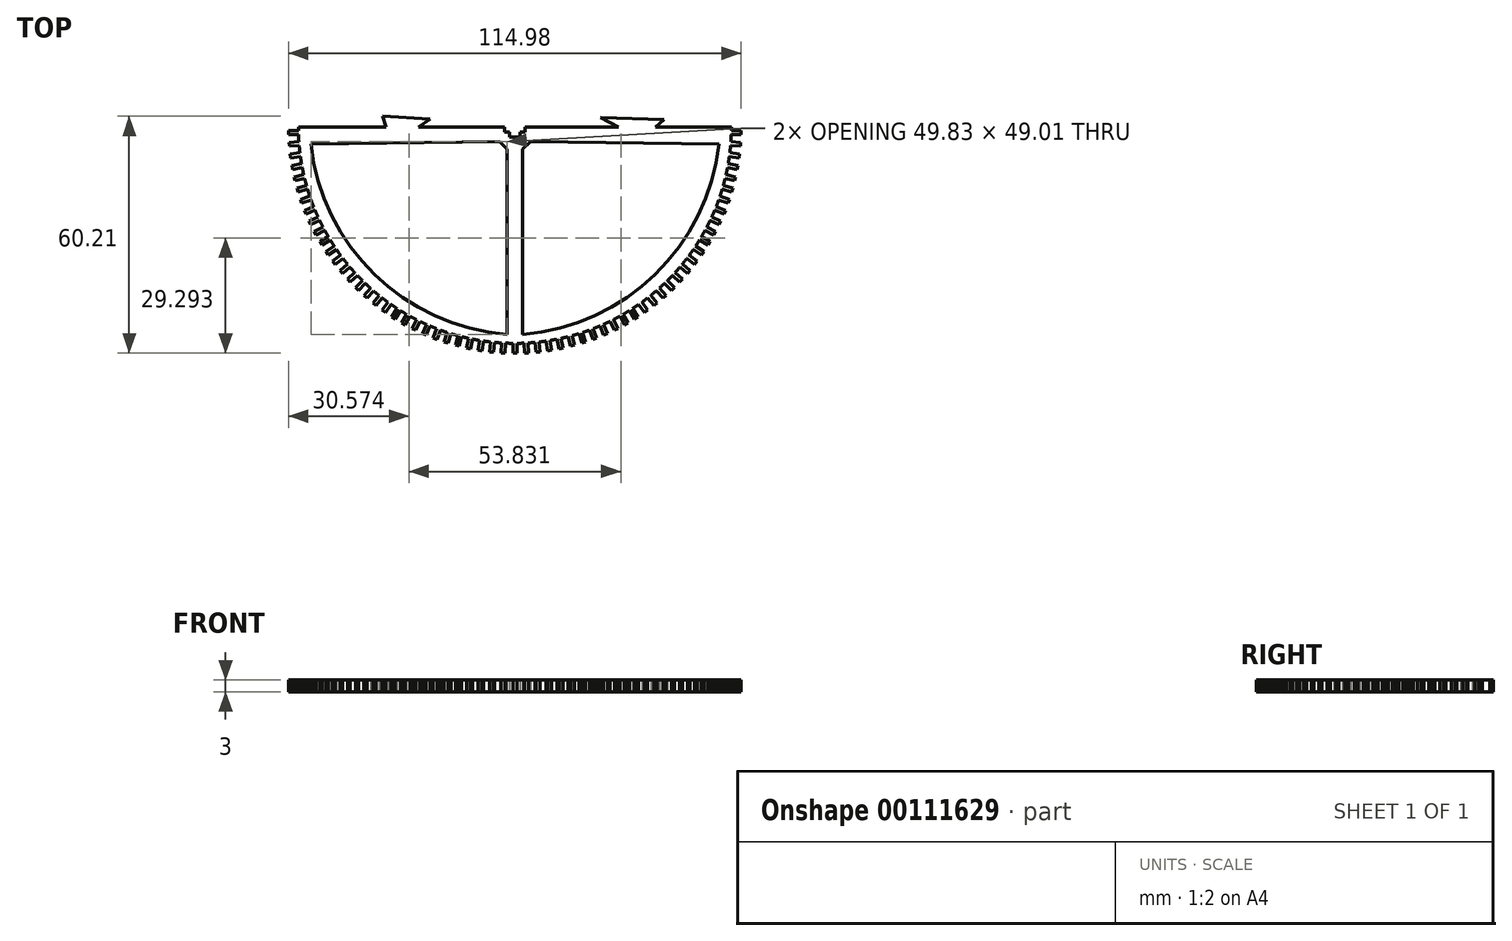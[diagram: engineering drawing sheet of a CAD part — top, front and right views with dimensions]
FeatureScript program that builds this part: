
annotation { "Feature Type Name" : "Feature", "Feature Type Description" : "" }
export const myFeature = defineFeature(function(context is Context, id is Id, definition is map)
    precondition{}
    {
        {
            var Q0;
            Q0=qCreatedBy(makeId("Top.planeOp"),FACE);
            var sketch = newSketch(context, id + "F0", { "sketchPlane" : qUnion([Q0])});
            skArc(sketch, "E0", {"start": v(-55, -0.92) * mm, "mid": v(0, -55) * mm, "end": v(55, -0.92) * mm});
            skLineSegment(sketch, "E1", {"start": v(2.6, -1.3) * mm, "end": v(1.3, -1.3) * mm});
            skLineSegment(sketch, "E2", {"start": v(1.3, -1.3) * mm, "end": v(1.3, -2.6) * mm});
            skLineSegment(sketch, "E3", {"start": v(1.3, -2.6) * mm, "end": v(0, -2.6) * mm});
            skLineSegment(sketch, "E4", {"start": v(0, -2.6) * mm, "end": v(-1.3, -2.6) * mm});
            skLineSegment(sketch, "E5", {"start": v(-1.3, -2.6) * mm, "end": v(-1.3, -1.3) * mm});
            skLineSegment(sketch, "E6", {"start": v(-1.3, -1.3) * mm, "end": v(-2.6, -1.3) * mm});
            skLineSegment(sketch, "E7", {"start": v(-2.6, -1.3) * mm, "end": v(-2.6, 0) * mm});
            skLineSegment(sketch, "E8", {"start": v(-3.92, -3.7) * mm, "end": v(-2, -5.66) * mm});
            skPoint(sketch, "E9.end.orphan", {"position": v(-1.3, -51.23) * mm});
            skPoint(sketch, "E9.start.orphan", {"position": v(0, -51.23) * mm});
            skLineSegment(sketch, "E10", {"start": v(-2, -50.71) * mm, "end": v(-2, -5.66) * mm});
            skPoint(sketch, "E11.start.orphan", {"position": v(0, -50.71) * mm});
            skLineSegment(sketch, "E12", {"start": v(-2, -50.71) * mm, "end": v(-2, -52.71) * mm});
            skArc(sketch, "E13", {"start": v(-51.83, -4.33) * mm, "mid": v(-35.63, -37.5) * mm, "end": v(-2, -52.71) * mm});
            skPoint(sketch, "E14.end.orphan", {"position": v(2, -50.71) * mm});
            skPoint(sketch, "E15.start.orphan", {"position": v(-51.96, 0) * mm});
            skLineSegment(sketch, "E16", {"start": v(-3.92, -3.7) * mm, "end": v(-51.83, -4.33) * mm});
            skPoint(sketch, "E16.endSnap0", {"position": v(-3.3, -4.33) * mm});
            skPoint(sketch, "E17.orphan", {"position": v(-4.62, -3) * mm});
            skLineSegment(sketch, "E18.MirrorCS", {"start": v(3.92, -3.7) * mm, "end": v(51.83, -4.33) * mm});
            skArc(sketch, "E19.MirrorCS", {"start": v(51.83, -4.33) * mm, "mid": v(35.63, -37.5) * mm, "end": v(2, -52.71) * mm});
            skLineSegment(sketch, "E20.MirrorCS", {"start": v(2, -50.71) * mm, "end": v(2, -5.66) * mm});
            skLineSegment(sketch, "E21.MirrorCS", {"start": v(3.92, -3.7) * mm, "end": v(2, -5.66) * mm});
            skLineSegment(sketch, "E22.MirrorCS", {"start": v(2, -50.71) * mm, "end": v(2, -52.71) * mm});
            skLineSegment(sketch, "E23.2.31.0", {"start": v(-57.5, -0.98) * mm, "end": v(-55, -0.92) * mm});
            skLineSegment(sketch, "E23.3.31.0", {"start": v(-57.47, -1.98) * mm, "end": v(-54.97, -1.92) * mm});
            skLineSegment(sketch, "E23.6.31.0", {"start": v(-57.48, -1.48) * mm, "end": v(-57.47, -1.98) * mm});
            skLineSegment(sketch, "E23.9.31.0", {"start": v(-57.48, -1.48) * mm, "end": v(-57.5, -0.98) * mm});
            skLineSegment(sketch, "E23.2.32.0", {"start": v(-57.37, -3.94) * mm, "end": v(-54.87, -3.75) * mm});
            skLineSegment(sketch, "E23.3.32.0", {"start": v(-57.29, -4.94) * mm, "end": v(-54.8, -4.74) * mm});
            skLineSegment(sketch, "E23.6.32.0", {"start": v(-57.33, -4.44) * mm, "end": v(-57.29, -4.94) * mm});
            skLineSegment(sketch, "E23.9.32.0", {"start": v(-57.33, -4.44) * mm, "end": v(-57.37, -3.94) * mm});
            skLineSegment(sketch, "E23.2.33.0", {"start": v(-57.09, -6.89) * mm, "end": v(-54.6, -6.57) * mm});
            skLineSegment(sketch, "E23.3.33.0", {"start": v(-56.96, -7.88) * mm, "end": v(-54.48, -7.56) * mm});
            skLineSegment(sketch, "E23.6.33.0", {"start": v(-57.02, -7.38) * mm, "end": v(-56.96, -7.88) * mm});
            skLineSegment(sketch, "E23.9.33.0", {"start": v(-57.02, -7.38) * mm, "end": v(-57.09, -6.89) * mm});
            skLineSegment(sketch, "E23.2.34.0", {"start": v(-56.66, -9.82) * mm, "end": v(-54.2, -9.37) * mm});
            skLineSegment(sketch, "E23.3.34.0", {"start": v(-56.48, -10.8) * mm, "end": v(-54.02, -10.35) * mm});
            skLineSegment(sketch, "E23.6.34.0", {"start": v(-56.57, -10.3) * mm, "end": v(-56.48, -10.8) * mm});
            skLineSegment(sketch, "E23.9.34.0", {"start": v(-56.57, -10.3) * mm, "end": v(-56.66, -9.82) * mm});
            skLineSegment(sketch, "E23.2.35.0", {"start": v(-56.08, -12.72) * mm, "end": v(-53.64, -12.15) * mm});
            skLineSegment(sketch, "E23.3.35.0", {"start": v(-55.85, -13.7) * mm, "end": v(-53.41, -13.12) * mm});
            skLineSegment(sketch, "E23.6.35.0", {"start": v(-55.96, -13.2) * mm, "end": v(-55.85, -13.7) * mm});
            skLineSegment(sketch, "E23.9.35.0", {"start": v(-55.96, -13.2) * mm, "end": v(-56.08, -12.72) * mm});
            skLineSegment(sketch, "E23.2.36.0", {"start": v(-55.35, -15.6) * mm, "end": v(-52.95, -14.9) * mm});
            skLineSegment(sketch, "E23.3.36.0", {"start": v(-55.07, -16.55) * mm, "end": v(-52.67, -15.85) * mm});
            skLineSegment(sketch, "E23.6.36.0", {"start": v(-55.2, -16.07) * mm, "end": v(-55.07, -16.55) * mm});
            skLineSegment(sketch, "E23.9.36.0", {"start": v(-55.2, -16.07) * mm, "end": v(-55.35, -15.6) * mm});
            skLineSegment(sketch, "E23.2.37.0", {"start": v(-54.47, -18.42) * mm, "end": v(-52.1, -17.6) * mm});
            skLineSegment(sketch, "E23.3.37.0", {"start": v(-54.14, -19.36) * mm, "end": v(-51.78, -18.54) * mm});
            skLineSegment(sketch, "E23.6.37.0", {"start": v(-54.3, -18.9) * mm, "end": v(-54.14, -19.36) * mm});
            skLineSegment(sketch, "E23.9.37.0", {"start": v(-54.3, -18.9) * mm, "end": v(-54.47, -18.42) * mm});
            skLineSegment(sketch, "E23.2.38.0", {"start": v(-53.45, -21.2) * mm, "end": v(-51.13, -20.26) * mm});
            skLineSegment(sketch, "E23.3.38.0", {"start": v(-53.08, -22.13) * mm, "end": v(-50.76, -21.18) * mm});
            skLineSegment(sketch, "E23.6.38.0", {"start": v(-53.26, -21.66) * mm, "end": v(-53.08, -22.13) * mm});
            skLineSegment(sketch, "E23.9.38.0", {"start": v(-53.26, -21.66) * mm, "end": v(-53.45, -21.2) * mm});
            skLineSegment(sketch, "E23.2.39.0", {"start": v(-52.29, -23.92) * mm, "end": v(-50.02, -22.86) * mm});
            skLineSegment(sketch, "E23.3.39.0", {"start": v(-51.87, -24.83) * mm, "end": v(-49.6, -23.77) * mm});
            skLineSegment(sketch, "E23.6.39.0", {"start": v(-52.08, -24.38) * mm, "end": v(-51.87, -24.83) * mm});
            skLineSegment(sketch, "E23.9.39.0", {"start": v(-52.08, -24.38) * mm, "end": v(-52.29, -23.92) * mm});
            skLineSegment(sketch, "E23.2.40.0", {"start": v(-50.99, -26.58) * mm, "end": v(-48.78, -25.4) * mm});
            skLineSegment(sketch, "E23.3.40.0", {"start": v(-50.52, -27.47) * mm, "end": v(-48.31, -26.29) * mm});
            skLineSegment(sketch, "E23.6.40.0", {"start": v(-50.75, -27.02) * mm, "end": v(-50.52, -27.47) * mm});
            skLineSegment(sketch, "E23.9.40.0", {"start": v(-50.75, -27.02) * mm, "end": v(-50.99, -26.58) * mm});
            skLineSegment(sketch, "E23.2.41.0", {"start": v(-49.55, -29.17) * mm, "end": v(-47.4, -27.88) * mm});
            skLineSegment(sketch, "E23.3.41.0", {"start": v(-49.04, -30.03) * mm, "end": v(-46.9, -28.74) * mm});
            skLineSegment(sketch, "E23.6.41.0", {"start": v(-49.3, -29.6) * mm, "end": v(-49.04, -30.03) * mm});
            skLineSegment(sketch, "E23.9.41.0", {"start": v(-49.3, -29.6) * mm, "end": v(-49.55, -29.17) * mm});
            skLineSegment(sketch, "E23.2.42.0", {"start": v(-47.99, -31.68) * mm, "end": v(-45.9, -30.29) * mm});
            skLineSegment(sketch, "E23.3.42.0", {"start": v(-47.43, -32.51) * mm, "end": v(-45.35, -31.12) * mm});
            skLineSegment(sketch, "E23.6.42.0", {"start": v(-47.7, -32.1) * mm, "end": v(-47.43, -32.51) * mm});
            skLineSegment(sketch, "E23.9.42.0", {"start": v(-47.7, -32.1) * mm, "end": v(-47.99, -31.68) * mm});
            skLineSegment(sketch, "E23.2.43.0", {"start": v(-46.3, -34.11) * mm, "end": v(-44.29, -32.61) * mm});
            skLineSegment(sketch, "E23.3.43.0", {"start": v(-45.7, -34.91) * mm, "end": v(-43.69, -33.41) * mm});
            skLineSegment(sketch, "E23.6.43.0", {"start": v(-46, -34.51) * mm, "end": v(-45.7, -34.91) * mm});
            skLineSegment(sketch, "E23.9.43.0", {"start": v(-46, -34.51) * mm, "end": v(-46.3, -34.11) * mm});
            skLineSegment(sketch, "E23.2.44.0", {"start": v(-44.47, -36.45) * mm, "end": v(-42.55, -34.85) * mm});
            skLineSegment(sketch, "E23.3.44.0", {"start": v(-43.83, -37.22) * mm, "end": v(-41.91, -35.62) * mm});
            skLineSegment(sketch, "E23.6.44.0", {"start": v(-44.15, -36.83) * mm, "end": v(-43.83, -37.22) * mm});
            skLineSegment(sketch, "E23.9.44.0", {"start": v(-44.15, -36.83) * mm, "end": v(-44.47, -36.45) * mm});
            skLineSegment(sketch, "E23.2.45.0", {"start": v(-42.54, -38.7) * mm, "end": v(-40.7, -37) * mm});
            skLineSegment(sketch, "E23.3.45.0", {"start": v(-41.86, -39.43) * mm, "end": v(-40.02, -37.73) * mm});
            skLineSegment(sketch, "E23.6.45.0", {"start": v(-42.2, -39.06) * mm, "end": v(-41.86, -39.43) * mm});
            skLineSegment(sketch, "E23.9.45.0", {"start": v(-42.2, -39.06) * mm, "end": v(-42.54, -38.7) * mm});
            skLineSegment(sketch, "E23.2.46.0", {"start": v(-40.49, -40.83) * mm, "end": v(-38.74, -39.04) * mm});
            skLineSegment(sketch, "E23.3.46.0", {"start": v(-39.77, -41.53) * mm, "end": v(-38.03, -39.74) * mm});
            skLineSegment(sketch, "E23.6.46.0", {"start": v(-40.13, -41.18) * mm, "end": v(-39.77, -41.53) * mm});
            skLineSegment(sketch, "E23.9.46.0", {"start": v(-40.13, -41.18) * mm, "end": v(-40.49, -40.83) * mm});
            skLineSegment(sketch, "E23.2.47.0", {"start": v(-38.33, -42.86) * mm, "end": v(-36.68, -40.98) * mm});
            skLineSegment(sketch, "E23.3.47.0", {"start": v(-37.58, -43.52) * mm, "end": v(-35.93, -41.64) * mm});
            skLineSegment(sketch, "E23.6.47.0", {"start": v(-37.96, -43.2) * mm, "end": v(-37.58, -43.52) * mm});
            skLineSegment(sketch, "E23.9.47.0", {"start": v(-37.96, -43.2) * mm, "end": v(-38.33, -42.86) * mm});
            skLineSegment(sketch, "E23.2.48.0", {"start": v(-36.08, -44.78) * mm, "end": v(-34.52, -42.81) * mm});
            skLineSegment(sketch, "E23.3.48.0", {"start": v(-35.3, -45.4) * mm, "end": v(-33.74, -43.44) * mm});
            skLineSegment(sketch, "E23.6.48.0", {"start": v(-35.69, -45.09) * mm, "end": v(-35.3, -45.4) * mm});
            skLineSegment(sketch, "E23.9.48.0", {"start": v(-35.69, -45.09) * mm, "end": v(-36.08, -44.78) * mm});
            skLineSegment(sketch, "E23.2.49.0", {"start": v(-33.72, -46.57) * mm, "end": v(-32.27, -44.53) * mm});
            skLineSegment(sketch, "E23.3.49.0", {"start": v(-32.9, -47.15) * mm, "end": v(-31.46, -45.11) * mm});
            skLineSegment(sketch, "E23.6.49.0", {"start": v(-33.32, -46.86) * mm, "end": v(-32.9, -47.15) * mm});
            skLineSegment(sketch, "E23.9.49.0", {"start": v(-33.32, -46.86) * mm, "end": v(-33.72, -46.57) * mm});
            skLineSegment(sketch, "E23.2.50.0", {"start": v(-31.28, -48.25) * mm, "end": v(-29.94, -46.14) * mm});
            skLineSegment(sketch, "E23.3.50.0", {"start": v(-30.44, -48.79) * mm, "end": v(-29.1, -46.67) * mm});
            skLineSegment(sketch, "E23.6.50.0", {"start": v(-30.86, -48.52) * mm, "end": v(-30.44, -48.79) * mm});
            skLineSegment(sketch, "E23.9.50.0", {"start": v(-30.86, -48.52) * mm, "end": v(-31.28, -48.25) * mm});
            skLineSegment(sketch, "E23.2.51.0", {"start": v(-28.76, -49.8) * mm, "end": v(-27.52, -47.62) * mm});
            skLineSegment(sketch, "E23.3.51.0", {"start": v(-27.89, -50.29) * mm, "end": v(-26.65, -48.1) * mm});
            skLineSegment(sketch, "E23.6.51.0", {"start": v(-28.32, -50.04) * mm, "end": v(-27.89, -50.29) * mm});
            skLineSegment(sketch, "E23.9.51.0", {"start": v(-28.32, -50.04) * mm, "end": v(-28.76, -49.8) * mm});
            skLineSegment(sketch, "E23.2.52.0", {"start": v(-26.16, -51.2) * mm, "end": v(-25.04, -48.97) * mm});
            skLineSegment(sketch, "E23.3.52.0", {"start": v(-25.26, -51.66) * mm, "end": v(-24.14, -49.42) * mm});
            skLineSegment(sketch, "E23.6.52.0", {"start": v(-25.7, -51.43) * mm, "end": v(-25.26, -51.66) * mm});
            skLineSegment(sketch, "E23.9.52.0", {"start": v(-25.7, -51.43) * mm, "end": v(-26.16, -51.2) * mm});
            skLineSegment(sketch, "E23.2.53.0", {"start": v(-23.48, -52.49) * mm, "end": v(-22.48, -50.2) * mm});
            skLineSegment(sketch, "E23.3.53.0", {"start": v(-22.57, -52.89) * mm, "end": v(-21.57, -50.6) * mm});
            skLineSegment(sketch, "E23.6.53.0", {"start": v(-23.03, -52.69) * mm, "end": v(-22.57, -52.89) * mm});
            skLineSegment(sketch, "E23.9.53.0", {"start": v(-23.03, -52.69) * mm, "end": v(-23.48, -52.49) * mm});
            skLineSegment(sketch, "E23.2.54.0", {"start": v(-20.75, -53.63) * mm, "end": v(-19.87, -51.29) * mm});
            skLineSegment(sketch, "E23.3.54.0", {"start": v(-19.82, -53.98) * mm, "end": v(-18.93, -51.64) * mm});
            skLineSegment(sketch, "E23.6.54.0", {"start": v(-20.28, -53.8) * mm, "end": v(-19.82, -53.98) * mm});
            skLineSegment(sketch, "E23.9.54.0", {"start": v(-20.28, -53.8) * mm, "end": v(-20.75, -53.63) * mm});
            skLineSegment(sketch, "E23.2.55.0", {"start": v(-17.96, -54.62) * mm, "end": v(-17.2, -52.24) * mm});
            skLineSegment(sketch, "E23.3.55.0", {"start": v(-17.01, -54.93) * mm, "end": v(-16.25, -52.54) * mm});
            skLineSegment(sketch, "E23.6.55.0", {"start": v(-17.49, -54.78) * mm, "end": v(-17.01, -54.93) * mm});
            skLineSegment(sketch, "E23.9.55.0", {"start": v(-17.49, -54.78) * mm, "end": v(-17.96, -54.62) * mm});
            skLineSegment(sketch, "E23.2.56.0", {"start": v(-15.13, -55.48) * mm, "end": v(-14.49, -53.06) * mm});
            skLineSegment(sketch, "E23.3.56.0", {"start": v(-14.16, -55.73) * mm, "end": v(-13.52, -53.31) * mm});
            skLineSegment(sketch, "E23.6.56.0", {"start": v(-14.64, -55.6) * mm, "end": v(-14.16, -55.73) * mm});
            skLineSegment(sketch, "E23.9.56.0", {"start": v(-14.64, -55.6) * mm, "end": v(-15.13, -55.48) * mm});
            skLineSegment(sketch, "E23.2.57.0", {"start": v(-12.25, -56.18) * mm, "end": v(-11.74, -53.73) * mm});
            skLineSegment(sketch, "E23.3.57.0", {"start": v(-11.27, -56.39) * mm, "end": v(-10.76, -53.94) * mm});
            skLineSegment(sketch, "E23.6.57.0", {"start": v(-11.76, -56.28) * mm, "end": v(-11.27, -56.39) * mm});
            skLineSegment(sketch, "E23.9.57.0", {"start": v(-11.76, -56.28) * mm, "end": v(-12.25, -56.18) * mm});
            skLineSegment(sketch, "E23.2.58.0", {"start": v(-9.34, -56.74) * mm, "end": v(-8.96, -54.27) * mm});
            skLineSegment(sketch, "E23.3.58.0", {"start": v(-8.35, -56.9) * mm, "end": v(-7.97, -54.42) * mm});
            skLineSegment(sketch, "E23.6.58.0", {"start": v(-8.85, -56.82) * mm, "end": v(-8.35, -56.9) * mm});
            skLineSegment(sketch, "E23.9.58.0", {"start": v(-8.85, -56.82) * mm, "end": v(-9.34, -56.74) * mm});
            skLineSegment(sketch, "E23.2.59.0", {"start": v(-6.4, -57.14) * mm, "end": v(-6.15, -54.65) * mm});
            skLineSegment(sketch, "E23.3.59.0", {"start": v(-5.41, -57.25) * mm, "end": v(-5.16, -54.76) * mm});
            skLineSegment(sketch, "E23.6.59.0", {"start": v(-5.91, -57.2) * mm, "end": v(-5.41, -57.25) * mm});
            skLineSegment(sketch, "E23.9.59.0", {"start": v(-5.91, -57.2) * mm, "end": v(-6.4, -57.14) * mm});
            skLineSegment(sketch, "E23.2.60.0", {"start": v(-3.46, -57.4) * mm, "end": v(-3.33, -54.9) * mm});
            skLineSegment(sketch, "E23.3.60.0", {"start": v(-2.46, -57.45) * mm, "end": v(-2.33, -54.95) * mm});
            skLineSegment(sketch, "E23.6.60.0", {"start": v(-2.96, -57.42) * mm, "end": v(-2.46, -57.45) * mm});
            skLineSegment(sketch, "E23.9.60.0", {"start": v(-2.96, -57.42) * mm, "end": v(-3.46, -57.4) * mm});
            skLineSegment(sketch, "E23.2.61.0", {"start": v(-0.5, -57.5) * mm, "end": v(-0.5, -55) * mm});
            skLineSegment(sketch, "E23.3.61.0", {"start": v(0.5, -57.5) * mm, "end": v(0.5, -55) * mm});
            skLineSegment(sketch, "E23.6.61.0", {"start": v(0, -57.5) * mm, "end": v(0.5, -57.5) * mm});
            skLineSegment(sketch, "E23.9.61.0", {"start": v(0, -57.5) * mm, "end": v(-0.5, -57.5) * mm});
            skLineSegment(sketch, "E23.2.62.0", {"start": v(2.46, -57.45) * mm, "end": v(2.33, -54.95) * mm});
            skLineSegment(sketch, "E23.3.62.0", {"start": v(3.46, -57.4) * mm, "end": v(3.33, -54.9) * mm});
            skLineSegment(sketch, "E23.6.62.0", {"start": v(2.96, -57.42) * mm, "end": v(3.46, -57.4) * mm});
            skLineSegment(sketch, "E23.9.62.0", {"start": v(2.96, -57.42) * mm, "end": v(2.46, -57.45) * mm});
            skLineSegment(sketch, "E23.2.63.0", {"start": v(5.41, -57.25) * mm, "end": v(5.16, -54.76) * mm});
            skLineSegment(sketch, "E23.3.63.0", {"start": v(6.4, -57.14) * mm, "end": v(6.15, -54.65) * mm});
            skLineSegment(sketch, "E23.6.63.0", {"start": v(5.91, -57.2) * mm, "end": v(6.4, -57.14) * mm});
            skLineSegment(sketch, "E23.9.63.0", {"start": v(5.91, -57.2) * mm, "end": v(5.41, -57.25) * mm});
            skLineSegment(sketch, "E23.2.64.0", {"start": v(8.35, -56.9) * mm, "end": v(7.97, -54.42) * mm});
            skLineSegment(sketch, "E23.3.64.0", {"start": v(9.34, -56.74) * mm, "end": v(8.96, -54.27) * mm});
            skLineSegment(sketch, "E23.6.64.0", {"start": v(8.85, -56.82) * mm, "end": v(9.34, -56.74) * mm});
            skLineSegment(sketch, "E23.9.64.0", {"start": v(8.85, -56.82) * mm, "end": v(8.35, -56.9) * mm});
            skLineSegment(sketch, "E23.2.65.0", {"start": v(11.27, -56.39) * mm, "end": v(10.76, -53.94) * mm});
            skLineSegment(sketch, "E23.3.65.0", {"start": v(12.25, -56.18) * mm, "end": v(11.74, -53.73) * mm});
            skLineSegment(sketch, "E23.6.65.0", {"start": v(11.76, -56.28) * mm, "end": v(12.25, -56.18) * mm});
            skLineSegment(sketch, "E23.9.65.0", {"start": v(11.76, -56.28) * mm, "end": v(11.27, -56.39) * mm});
            skLineSegment(sketch, "E23.2.66.0", {"start": v(14.16, -55.73) * mm, "end": v(13.52, -53.31) * mm});
            skLineSegment(sketch, "E23.3.66.0", {"start": v(15.13, -55.48) * mm, "end": v(14.49, -53.06) * mm});
            skLineSegment(sketch, "E23.6.66.0", {"start": v(14.64, -55.6) * mm, "end": v(15.13, -55.48) * mm});
            skLineSegment(sketch, "E23.9.66.0", {"start": v(14.64, -55.6) * mm, "end": v(14.16, -55.73) * mm});
            skLineSegment(sketch, "E23.2.67.0", {"start": v(17.01, -54.93) * mm, "end": v(16.25, -52.54) * mm});
            skLineSegment(sketch, "E23.3.67.0", {"start": v(17.96, -54.62) * mm, "end": v(17.2, -52.24) * mm});
            skLineSegment(sketch, "E23.6.67.0", {"start": v(17.49, -54.78) * mm, "end": v(17.96, -54.62) * mm});
            skLineSegment(sketch, "E23.9.67.0", {"start": v(17.49, -54.78) * mm, "end": v(17.01, -54.93) * mm});
            skLineSegment(sketch, "E23.2.68.0", {"start": v(19.82, -53.98) * mm, "end": v(18.93, -51.64) * mm});
            skLineSegment(sketch, "E23.3.68.0", {"start": v(20.75, -53.63) * mm, "end": v(19.87, -51.29) * mm});
            skLineSegment(sketch, "E23.6.68.0", {"start": v(20.28, -53.8) * mm, "end": v(20.75, -53.63) * mm});
            skLineSegment(sketch, "E23.9.68.0", {"start": v(20.28, -53.8) * mm, "end": v(19.82, -53.98) * mm});
            skLineSegment(sketch, "E23.2.69.0", {"start": v(22.57, -52.89) * mm, "end": v(21.57, -50.6) * mm});
            skLineSegment(sketch, "E23.3.69.0", {"start": v(23.48, -52.49) * mm, "end": v(22.48, -50.2) * mm});
            skLineSegment(sketch, "E23.6.69.0", {"start": v(23.03, -52.69) * mm, "end": v(23.48, -52.49) * mm});
            skLineSegment(sketch, "E23.9.69.0", {"start": v(23.03, -52.69) * mm, "end": v(22.57, -52.89) * mm});
            skLineSegment(sketch, "E23.2.70.0", {"start": v(25.26, -51.66) * mm, "end": v(24.14, -49.42) * mm});
            skLineSegment(sketch, "E23.3.70.0", {"start": v(26.16, -51.2) * mm, "end": v(25.04, -48.97) * mm});
            skLineSegment(sketch, "E23.6.70.0", {"start": v(25.7, -51.43) * mm, "end": v(26.16, -51.2) * mm});
            skLineSegment(sketch, "E23.9.70.0", {"start": v(25.7, -51.43) * mm, "end": v(25.26, -51.66) * mm});
            skLineSegment(sketch, "E23.2.71.0", {"start": v(27.89, -50.29) * mm, "end": v(26.65, -48.1) * mm});
            skLineSegment(sketch, "E23.3.71.0", {"start": v(28.76, -49.8) * mm, "end": v(27.52, -47.62) * mm});
            skLineSegment(sketch, "E23.6.71.0", {"start": v(28.32, -50.04) * mm, "end": v(28.76, -49.8) * mm});
            skLineSegment(sketch, "E23.9.71.0", {"start": v(28.32, -50.04) * mm, "end": v(27.89, -50.29) * mm});
            skLineSegment(sketch, "E23.2.72.0", {"start": v(30.44, -48.79) * mm, "end": v(29.1, -46.67) * mm});
            skLineSegment(sketch, "E23.3.72.0", {"start": v(31.28, -48.25) * mm, "end": v(29.94, -46.14) * mm});
            skLineSegment(sketch, "E23.6.72.0", {"start": v(30.86, -48.52) * mm, "end": v(31.28, -48.25) * mm});
            skLineSegment(sketch, "E23.9.72.0", {"start": v(30.86, -48.52) * mm, "end": v(30.44, -48.79) * mm});
            skLineSegment(sketch, "E23.2.73.0", {"start": v(32.9, -47.15) * mm, "end": v(31.46, -45.11) * mm});
            skLineSegment(sketch, "E23.3.73.0", {"start": v(33.72, -46.57) * mm, "end": v(32.27, -44.53) * mm});
            skLineSegment(sketch, "E23.6.73.0", {"start": v(33.32, -46.86) * mm, "end": v(33.72, -46.57) * mm});
            skLineSegment(sketch, "E23.9.73.0", {"start": v(33.32, -46.86) * mm, "end": v(32.9, -47.15) * mm});
            skLineSegment(sketch, "E23.2.74.0", {"start": v(35.3, -45.4) * mm, "end": v(33.74, -43.44) * mm});
            skLineSegment(sketch, "E23.3.74.0", {"start": v(36.08, -44.78) * mm, "end": v(34.52, -42.81) * mm});
            skLineSegment(sketch, "E23.6.74.0", {"start": v(35.69, -45.09) * mm, "end": v(36.08, -44.78) * mm});
            skLineSegment(sketch, "E23.9.74.0", {"start": v(35.69, -45.09) * mm, "end": v(35.3, -45.4) * mm});
            skLineSegment(sketch, "E23.2.75.0", {"start": v(37.58, -43.52) * mm, "end": v(35.93, -41.64) * mm});
            skLineSegment(sketch, "E23.3.75.0", {"start": v(38.33, -42.86) * mm, "end": v(36.68, -40.98) * mm});
            skLineSegment(sketch, "E23.6.75.0", {"start": v(37.96, -43.2) * mm, "end": v(38.33, -42.86) * mm});
            skLineSegment(sketch, "E23.9.75.0", {"start": v(37.96, -43.2) * mm, "end": v(37.58, -43.52) * mm});
            skLineSegment(sketch, "E23.2.76.0", {"start": v(39.77, -41.53) * mm, "end": v(38.03, -39.74) * mm});
            skLineSegment(sketch, "E23.3.76.0", {"start": v(40.49, -40.83) * mm, "end": v(38.74, -39.04) * mm});
            skLineSegment(sketch, "E23.6.76.0", {"start": v(40.13, -41.18) * mm, "end": v(40.49, -40.83) * mm});
            skLineSegment(sketch, "E23.9.76.0", {"start": v(40.13, -41.18) * mm, "end": v(39.77, -41.53) * mm});
            skLineSegment(sketch, "E23.2.77.0", {"start": v(41.86, -39.43) * mm, "end": v(40.02, -37.73) * mm});
            skLineSegment(sketch, "E23.3.77.0", {"start": v(42.54, -38.7) * mm, "end": v(40.7, -37) * mm});
            skLineSegment(sketch, "E23.6.77.0", {"start": v(42.2, -39.06) * mm, "end": v(42.54, -38.7) * mm});
            skLineSegment(sketch, "E23.9.77.0", {"start": v(42.2, -39.06) * mm, "end": v(41.86, -39.43) * mm});
            skLineSegment(sketch, "E23.2.78.0", {"start": v(43.83, -37.22) * mm, "end": v(41.91, -35.62) * mm});
            skLineSegment(sketch, "E23.3.78.0", {"start": v(44.47, -36.45) * mm, "end": v(42.55, -34.85) * mm});
            skLineSegment(sketch, "E23.6.78.0", {"start": v(44.15, -36.83) * mm, "end": v(44.47, -36.45) * mm});
            skLineSegment(sketch, "E23.9.78.0", {"start": v(44.15, -36.83) * mm, "end": v(43.83, -37.22) * mm});
            skLineSegment(sketch, "E23.2.79.0", {"start": v(45.7, -34.91) * mm, "end": v(43.69, -33.41) * mm});
            skLineSegment(sketch, "E23.3.79.0", {"start": v(46.3, -34.11) * mm, "end": v(44.29, -32.61) * mm});
            skLineSegment(sketch, "E23.6.79.0", {"start": v(46, -34.51) * mm, "end": v(46.3, -34.11) * mm});
            skLineSegment(sketch, "E23.9.79.0", {"start": v(46, -34.51) * mm, "end": v(45.7, -34.91) * mm});
            skLineSegment(sketch, "E23.2.80.0", {"start": v(47.43, -32.51) * mm, "end": v(45.35, -31.12) * mm});
            skLineSegment(sketch, "E23.3.80.0", {"start": v(47.99, -31.68) * mm, "end": v(45.9, -30.29) * mm});
            skLineSegment(sketch, "E23.6.80.0", {"start": v(47.7, -32.1) * mm, "end": v(47.99, -31.68) * mm});
            skLineSegment(sketch, "E23.9.80.0", {"start": v(47.7, -32.1) * mm, "end": v(47.43, -32.51) * mm});
            skLineSegment(sketch, "E23.2.81.0", {"start": v(49.04, -30.03) * mm, "end": v(46.9, -28.74) * mm});
            skLineSegment(sketch, "E23.3.81.0", {"start": v(49.55, -29.17) * mm, "end": v(47.4, -27.88) * mm});
            skLineSegment(sketch, "E23.6.81.0", {"start": v(49.3, -29.6) * mm, "end": v(49.55, -29.17) * mm});
            skLineSegment(sketch, "E23.9.81.0", {"start": v(49.3, -29.6) * mm, "end": v(49.04, -30.03) * mm});
            skLineSegment(sketch, "E23.2.82.0", {"start": v(50.52, -27.47) * mm, "end": v(48.31, -26.29) * mm});
            skLineSegment(sketch, "E23.3.82.0", {"start": v(50.99, -26.58) * mm, "end": v(48.78, -25.4) * mm});
            skLineSegment(sketch, "E23.6.82.0", {"start": v(50.75, -27.02) * mm, "end": v(50.99, -26.58) * mm});
            skLineSegment(sketch, "E23.9.82.0", {"start": v(50.75, -27.02) * mm, "end": v(50.52, -27.47) * mm});
            skLineSegment(sketch, "E23.2.83.0", {"start": v(51.87, -24.83) * mm, "end": v(49.6, -23.77) * mm});
            skLineSegment(sketch, "E23.3.83.0", {"start": v(52.29, -23.92) * mm, "end": v(50.02, -22.86) * mm});
            skLineSegment(sketch, "E23.6.83.0", {"start": v(52.08, -24.38) * mm, "end": v(52.29, -23.92) * mm});
            skLineSegment(sketch, "E23.9.83.0", {"start": v(52.08, -24.38) * mm, "end": v(51.87, -24.83) * mm});
            skLineSegment(sketch, "E23.2.84.0", {"start": v(53.08, -22.13) * mm, "end": v(50.76, -21.18) * mm});
            skLineSegment(sketch, "E23.3.84.0", {"start": v(53.45, -21.2) * mm, "end": v(51.13, -20.26) * mm});
            skLineSegment(sketch, "E23.6.84.0", {"start": v(53.26, -21.66) * mm, "end": v(53.45, -21.2) * mm});
            skLineSegment(sketch, "E23.9.84.0", {"start": v(53.26, -21.66) * mm, "end": v(53.08, -22.13) * mm});
            skLineSegment(sketch, "E23.2.85.0", {"start": v(54.14, -19.36) * mm, "end": v(51.78, -18.54) * mm});
            skLineSegment(sketch, "E23.3.85.0", {"start": v(54.47, -18.42) * mm, "end": v(52.1, -17.6) * mm});
            skLineSegment(sketch, "E23.6.85.0", {"start": v(54.3, -18.9) * mm, "end": v(54.47, -18.42) * mm});
            skLineSegment(sketch, "E23.9.85.0", {"start": v(54.3, -18.9) * mm, "end": v(54.14, -19.36) * mm});
            skLineSegment(sketch, "E23.2.86.0", {"start": v(55.07, -16.55) * mm, "end": v(52.67, -15.85) * mm});
            skLineSegment(sketch, "E23.3.86.0", {"start": v(55.35, -15.6) * mm, "end": v(52.95, -14.9) * mm});
            skLineSegment(sketch, "E23.6.86.0", {"start": v(55.2, -16.07) * mm, "end": v(55.35, -15.6) * mm});
            skLineSegment(sketch, "E23.9.86.0", {"start": v(55.2, -16.07) * mm, "end": v(55.07, -16.55) * mm});
            skLineSegment(sketch, "E23.2.87.0", {"start": v(55.85, -13.7) * mm, "end": v(53.41, -13.12) * mm});
            skLineSegment(sketch, "E23.3.87.0", {"start": v(56.08, -12.72) * mm, "end": v(53.64, -12.15) * mm});
            skLineSegment(sketch, "E23.6.87.0", {"start": v(55.96, -13.2) * mm, "end": v(56.08, -12.72) * mm});
            skLineSegment(sketch, "E23.9.87.0", {"start": v(55.96, -13.2) * mm, "end": v(55.85, -13.7) * mm});
            skLineSegment(sketch, "E23.2.88.0", {"start": v(56.48, -10.8) * mm, "end": v(54.02, -10.35) * mm});
            skLineSegment(sketch, "E23.3.88.0", {"start": v(56.66, -9.82) * mm, "end": v(54.2, -9.37) * mm});
            skLineSegment(sketch, "E23.6.88.0", {"start": v(56.57, -10.3) * mm, "end": v(56.66, -9.82) * mm});
            skLineSegment(sketch, "E23.9.88.0", {"start": v(56.57, -10.3) * mm, "end": v(56.48, -10.8) * mm});
            skLineSegment(sketch, "E23.2.89.0", {"start": v(56.96, -7.88) * mm, "end": v(54.48, -7.56) * mm});
            skLineSegment(sketch, "E23.3.89.0", {"start": v(57.09, -6.89) * mm, "end": v(54.6, -6.57) * mm});
            skLineSegment(sketch, "E23.6.89.0", {"start": v(57.02, -7.38) * mm, "end": v(57.09, -6.89) * mm});
            skLineSegment(sketch, "E23.9.89.0", {"start": v(57.02, -7.38) * mm, "end": v(56.96, -7.88) * mm});
            skLineSegment(sketch, "E23.2.90.0", {"start": v(57.29, -4.94) * mm, "end": v(54.8, -4.74) * mm});
            skLineSegment(sketch, "E23.3.90.0", {"start": v(57.37, -3.94) * mm, "end": v(54.87, -3.75) * mm});
            skLineSegment(sketch, "E23.6.90.0", {"start": v(57.33, -4.44) * mm, "end": v(57.37, -3.94) * mm});
            skLineSegment(sketch, "E23.9.90.0", {"start": v(57.33, -4.44) * mm, "end": v(57.29, -4.94) * mm});
            skLineSegment(sketch, "E23.2.91.0", {"start": v(57.47, -1.98) * mm, "end": v(54.97, -1.92) * mm});
            skLineSegment(sketch, "E23.3.91.0", {"start": v(57.5, -0.98) * mm, "end": v(55, -0.92) * mm});
            skLineSegment(sketch, "E23.6.91.0", {"start": v(57.48, -1.48) * mm, "end": v(57.5, -0.98) * mm});
            skLineSegment(sketch, "E23.9.91.0", {"start": v(57.48, -1.48) * mm, "end": v(57.47, -1.98) * mm});
            skLineSegment(sketch, "E24", {"start": v(-51.96, 0) * mm, "end": v(-32.7, 0) * mm});
            skLineSegment(sketch, "E25", {"start": v(35.68, 0) * mm, "end": v(37.88, 1.86) * mm});
            skLineSegment(sketch, "E26", {"start": v(37.88, 1.86) * mm, "end": v(21.75, 2.38) * mm});
            skLineSegment(sketch, "E27", {"start": v(21.75, 2.38) * mm, "end": v(26.37, 0) * mm});
            skLineSegment(sketch, "E28", {"start": v(-24.52, 0) * mm, "end": v(-21.56, 2.01) * mm});
            skLineSegment(sketch, "E29", {"start": v(-21.56, 2.01) * mm, "end": v(-33.67, 2.7) * mm});
            skLineSegment(sketch, "E30", {"start": v(-33.67, 2.7) * mm, "end": v(-32.7, 0) * mm});
            skLineSegment(sketch, "E31.trimOffspring", {"start": v(35.68, 0) * mm, "end": v(55, 0) * mm});
            skLineSegment(sketch, "E32", {"start": v(55, -0.92) * mm, "end": v(55, 0) * mm});
            skLineSegment(sketch, "E33", {"start": v(-55, -0.92) * mm, "end": v(-55, 0) * mm});
            skLineSegment(sketch, "E34.trimOffspring", {"start": v(2.6, 0) * mm, "end": v(26.37, 0) * mm});
            skPoint(sketch, "E35.start.orphan", {"position": v(2.6, 0) * mm});
            skLineSegment(sketch, "E36", {"start": v(2.6, -1.3) * mm, "end": v(2.6, 0) * mm});
            skLineSegment(sketch, "E37", {"start": v(-51.96, 0) * mm, "end": v(-55, 0) * mm});
            skLineSegment(sketch, "E38", {"start": v(-2.6, 0) * mm, "end": v(-24.52, 0) * mm});
            skLineSegment(sketch, "E39", {"start": v(0, -2.6) * mm, "end": v(0, -5.66) * mm});
            skSolve(sketch);
        }
        {
            var Q0;
            Q0 = qSketchRegion(id + "F0", true);
            extrude(context, id + "F1", {"entities" : qUnion([Q0]), "depth" : 3 * mm});
        }
    });
